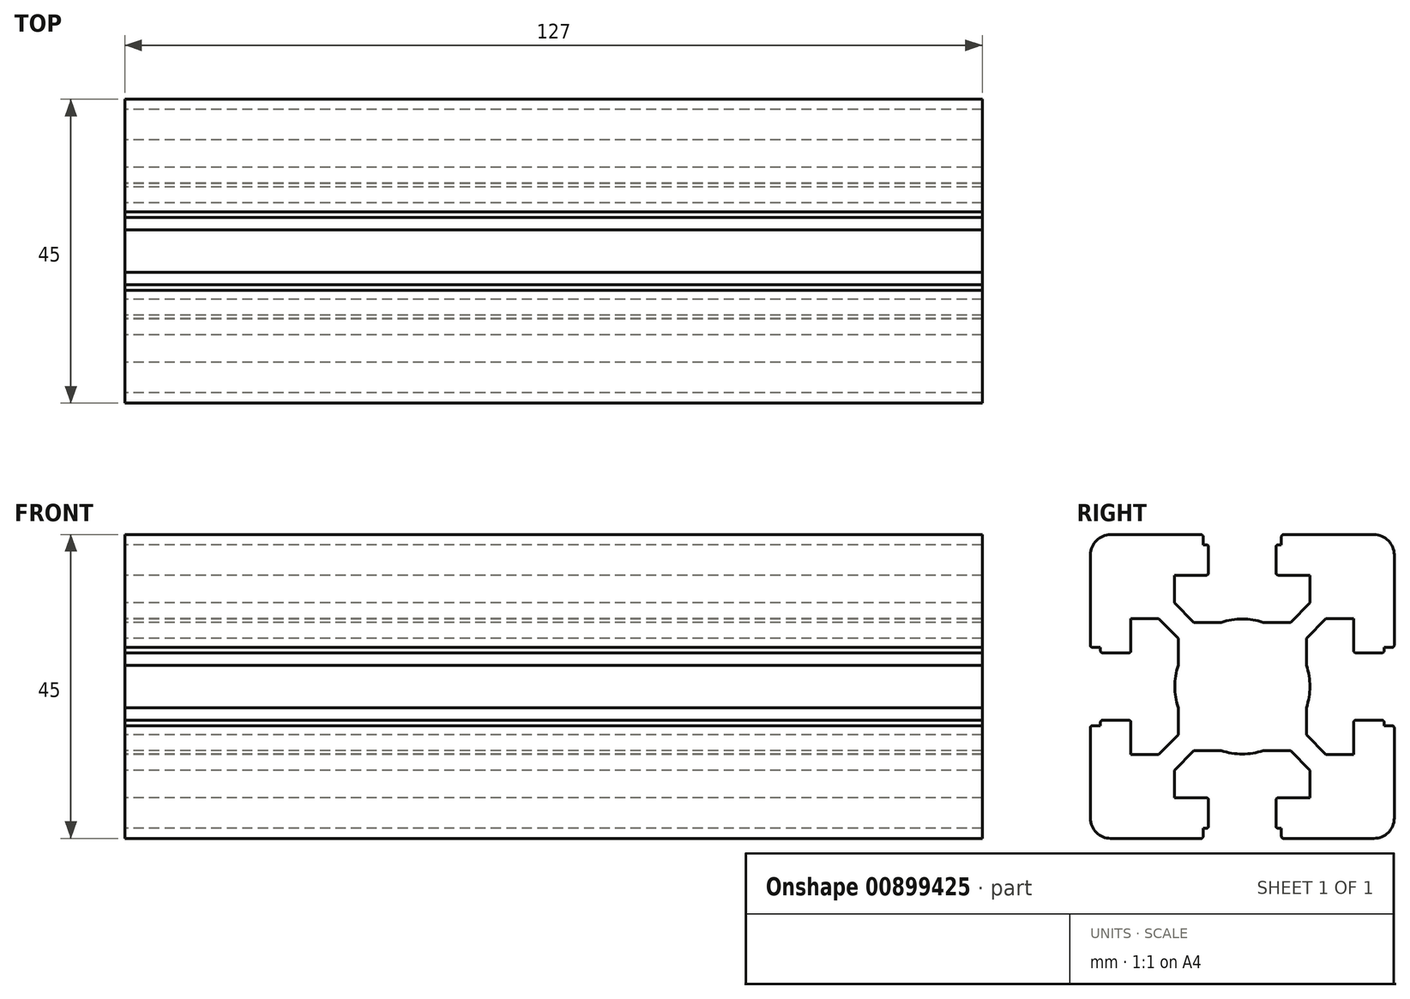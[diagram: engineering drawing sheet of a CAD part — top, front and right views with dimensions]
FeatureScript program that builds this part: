
annotation { "Feature Type Name" : "Feature", "Feature Type Description" : "" }
export const myFeature = defineFeature(function(context is Context, id is Id, definition is map)
    precondition{}
    {
        {
            var Q0;
            Q0=qCreatedBy(makeId("Right.planeOp"),FACE);
            var sketch = newSketch(context, id + "F0", { "sketchPlane" : qUnion([Q0])});
            skLineSegment(sketch, "E0", {"start": v(-20.09, -10.29) * mm, "end": v(-21.29, -10.29) * mm});
            skArc(sketch, "E1", {"start": v(-21.29, -10.29) * mm, "mid": v(-21.5, -10.38) * mm, "end": v(-21.59, -10.59) * mm});
            skLineSegment(sketch, "E2", {"start": v(-21.59, -10.59) * mm, "end": v(-21.59, -23.99) * mm});
            skArc(sketch, "E3", {"start": v(-21.59, -23.99) * mm, "mid": v(-20.7, -26.11) * mm, "end": v(-18.59, -26.99) * mm});
            skLineSegment(sketch, "E4", {"start": v(-18.59, -26.99) * mm, "end": v(-5.19, -26.99) * mm});
            skArc(sketch, "E5", {"start": v(-5.19, -26.99) * mm, "mid": v(-4.98, -26.9) * mm, "end": v(-4.89, -26.69) * mm});
            skLineSegment(sketch, "E6", {"start": v(-4.89, -26.69) * mm, "end": v(-4.89, -25.49) * mm});
            skLineSegment(sketch, "E7", {"start": v(-4.89, -25.49) * mm, "end": v(-4.39, -25.49) * mm});
            skArc(sketch, "E8", {"start": v(-4.39, -25.49) * mm, "mid": v(-4.18, -25.4) * mm, "end": v(-4.09, -25.19) * mm});
            skLineSegment(sketch, "E9", {"start": v(-4.09, -25.19) * mm, "end": v(-4.09, -21.29) * mm});
            skArc(sketch, "E10", {"start": v(-4.09, -21.29) * mm, "mid": v(-4.18, -21.08) * mm, "end": v(-4.39, -20.99) * mm});
            skLineSegment(sketch, "E11", {"start": v(-4.39, -20.99) * mm, "end": v(-9.14, -20.99) * mm});
            skLineSegment(sketch, "E12", {"start": v(-9.14, -20.99) * mm, "end": v(-9.14, -16.88) * mm});
            skLineSegment(sketch, "E13", {"start": v(-9.14, -16.88) * mm, "end": v(-6.25, -13.99) * mm});
            skLineSegment(sketch, "E14", {"start": v(-6.25, -13.99) * mm, "end": v(-2.21, -13.99) * mm});
            skArc(sketch, "E15", {"start": v(-2.21, -13.99) * mm, "mid": v(0.91, -14.49) * mm, "end": v(4.03, -13.99) * mm});
            skLineSegment(sketch, "E16", {"start": v(-20.09, -10.29) * mm, "end": v(-20.09, -9.79) * mm});
            skArc(sketch, "E17", {"start": v(-20.09, -9.79) * mm, "mid": v(-20, -9.58) * mm, "end": v(-19.79, -9.49) * mm});
            skLineSegment(sketch, "E18", {"start": v(-19.79, -9.49) * mm, "end": v(-15.89, -9.49) * mm});
            skArc(sketch, "E19", {"start": v(-15.89, -9.49) * mm, "mid": v(-15.68, -9.58) * mm, "end": v(-15.59, -9.79) * mm});
            skLineSegment(sketch, "E20", {"start": v(-15.59, -9.79) * mm, "end": v(-15.59, -14.54) * mm});
            skLineSegment(sketch, "E21", {"start": v(-15.59, -14.54) * mm, "end": v(-11.48, -14.54) * mm});
            skLineSegment(sketch, "E22", {"start": v(-11.48, -14.54) * mm, "end": v(-8.59, -11.65) * mm});
            skLineSegment(sketch, "E23", {"start": v(-8.59, -11.65) * mm, "end": v(-8.59, -7.61) * mm});
            skLineSegment(sketch, "E24", {"start": v(29.82, -4.49) * mm, "end": v(-31.05, -4.49) * mm});
            skLineSegment(sketch, "E25.MirrorCS", {"start": v(6.71, -25.49) * mm, "end": v(6.21, -25.49) * mm});
            skArc(sketch, "E26.MirrorCS", {"start": v(7.01, -26.99) * mm, "mid": v(6.8, -26.9) * mm, "end": v(6.71, -26.69) * mm});
            skLineSegment(sketch, "E27.MirrorCS", {"start": v(10.41, -11.65) * mm, "end": v(10.41, -7.61) * mm});
            skArc(sketch, "E28.MirrorCS", {"start": v(6.21, -25.49) * mm, "mid": v(6, -25.4) * mm, "end": v(5.91, -25.19) * mm});
            skLineSegment(sketch, "E29.MirrorCS", {"start": v(6.71, -26.69) * mm, "end": v(6.71, -25.49) * mm});
            skArc(sketch, "E30.MirrorCS", {"start": v(5.91, -21.29) * mm, "mid": v(6, -21.08) * mm, "end": v(6.21, -20.99) * mm});
            skLineSegment(sketch, "E31.MirrorCS", {"start": v(10.96, -16.88) * mm, "end": v(8.07, -13.99) * mm});
            skLineSegment(sketch, "E32.MirrorCS", {"start": v(13.3, -14.54) * mm, "end": v(10.41, -11.65) * mm});
            skLineSegment(sketch, "E33.MirrorCS", {"start": v(17.41, -14.54) * mm, "end": v(13.3, -14.54) * mm});
            skLineSegment(sketch, "E34.MirrorCS", {"start": v(17.41, -9.79) * mm, "end": v(17.41, -14.54) * mm});
            skLineSegment(sketch, "E35.MirrorCS", {"start": v(6.21, -20.99) * mm, "end": v(10.96, -20.99) * mm});
            skLineSegment(sketch, "E36.MirrorCS", {"start": v(8.07, -13.99) * mm, "end": v(4.03, -13.99) * mm});
            skArc(sketch, "E37.MirrorCS", {"start": v(4.03, -13.99) * mm, "mid": v(0.91, -14.49) * mm, "end": v(-2.21, -13.99) * mm});
            skLineSegment(sketch, "E38.MirrorCS", {"start": v(10.96, -20.99) * mm, "end": v(10.96, -16.88) * mm});
            skLineSegment(sketch, "E39.MirrorCS", {"start": v(5.91, -25.19) * mm, "end": v(5.91, -21.29) * mm});
            skArc(sketch, "E40.MirrorCS", {"start": v(23.41, -23.99) * mm, "mid": v(22.53, -26.11) * mm, "end": v(20.41, -26.99) * mm});
            skLineSegment(sketch, "E41.MirrorCS", {"start": v(20.41, -26.99) * mm, "end": v(7.01, -26.99) * mm});
            skLineSegment(sketch, "E42.MirrorCS", {"start": v(23.41, -10.59) * mm, "end": v(23.41, -23.99) * mm});
            skArc(sketch, "E43.MirrorCS", {"start": v(17.71, -9.49) * mm, "mid": v(17.5, -9.58) * mm, "end": v(17.41, -9.79) * mm});
            skArc(sketch, "E44.MirrorCS", {"start": v(23.11, -10.29) * mm, "mid": v(23.32, -10.38) * mm, "end": v(23.41, -10.59) * mm});
            skLineSegment(sketch, "E45.MirrorCS", {"start": v(21.91, -10.29) * mm, "end": v(21.91, -9.79) * mm});
            skLineSegment(sketch, "E46.MirrorCS", {"start": v(21.91, -10.29) * mm, "end": v(23.11, -10.29) * mm});
            skArc(sketch, "E47.MirrorCS", {"start": v(21.91, -9.79) * mm, "mid": v(21.82, -9.58) * mm, "end": v(21.61, -9.49) * mm});
            skLineSegment(sketch, "E48.MirrorCS", {"start": v(21.61, -9.49) * mm, "end": v(17.71, -9.49) * mm});
            skLineSegment(sketch, "E49.MirrorCS", {"start": v(6.71, 16.51) * mm, "end": v(6.21, 16.51) * mm});
            skArc(sketch, "E50.MirrorCS", {"start": v(-4.39, 16.51) * mm, "mid": v(-4.18, 16.42) * mm, "end": v(-4.09, 16.21) * mm});
            skLineSegment(sketch, "E51.MirrorCS", {"start": v(-4.89, 16.51) * mm, "end": v(-4.39, 16.51) * mm});
            skArc(sketch, "E52.MirrorCS", {"start": v(5.91, 12.31) * mm, "mid": v(6, 12.1) * mm, "end": v(6.21, 12.01) * mm});
            skLineSegment(sketch, "E53.MirrorCS", {"start": v(6.71, 17.71) * mm, "end": v(6.71, 16.51) * mm});
            skLineSegment(sketch, "E54.MirrorCS", {"start": v(-4.89, 17.71) * mm, "end": v(-4.89, 16.51) * mm});
            skArc(sketch, "E55.MirrorCS", {"start": v(-5.19, 18.01) * mm, "mid": v(-4.98, 17.92) * mm, "end": v(-4.89, 17.71) * mm});
            skArc(sketch, "E56.MirrorCS", {"start": v(-4.09, 12.31) * mm, "mid": v(-4.18, 12.1) * mm, "end": v(-4.39, 12.01) * mm});
            skArc(sketch, "E57.MirrorCS", {"start": v(7.01, 18.01) * mm, "mid": v(6.8, 17.92) * mm, "end": v(6.71, 17.71) * mm});
            skArc(sketch, "E58.MirrorCS", {"start": v(6.21, 16.51) * mm, "mid": v(6, 16.42) * mm, "end": v(5.91, 16.21) * mm});
            skArc(sketch, "E59.MirrorCS", {"start": v(23.11, 1.31) * mm, "mid": v(23.32, 1.4) * mm, "end": v(23.41, 1.61) * mm});
            skLineSegment(sketch, "E60.MirrorCS", {"start": v(21.91, 1.31) * mm, "end": v(21.91, 0.81) * mm});
            skArc(sketch, "E61.MirrorCS", {"start": v(-15.89, 0.51) * mm, "mid": v(-15.68, 0.6) * mm, "end": v(-15.59, 0.81) * mm});
            skArc(sketch, "E62.MirrorCS", {"start": v(-21.29, 1.31) * mm, "mid": v(-21.5, 1.4) * mm, "end": v(-21.59, 1.61) * mm});
            skArc(sketch, "E63.MirrorCS", {"start": v(17.71, 0.51) * mm, "mid": v(17.5, 0.6) * mm, "end": v(17.41, 0.81) * mm});
            skArc(sketch, "E64.MirrorCS", {"start": v(21.91, 0.81) * mm, "mid": v(21.82, 0.6) * mm, "end": v(21.61, 0.51) * mm});
            skLineSegment(sketch, "E65.MirrorCS", {"start": v(21.91, 1.31) * mm, "end": v(23.11, 1.31) * mm});
            skArc(sketch, "E66.MirrorCS", {"start": v(14.31, 5.31) * mm, "mid": v(14.1, 5.4) * mm, "end": v(14.01, 5.61) * mm});
            skArc(sketch, "E67.MirrorCS", {"start": v(-20.09, 0.81) * mm, "mid": v(-20, 0.6) * mm, "end": v(-19.79, 0.51) * mm});
            skLineSegment(sketch, "E68.MirrorCS", {"start": v(-20.09, 1.31) * mm, "end": v(-21.29, 1.31) * mm});
            skLineSegment(sketch, "E69.MirrorCS", {"start": v(-20.09, 1.31) * mm, "end": v(-20.09, 0.81) * mm});
            skLineSegment(sketch, "E70.MirrorCS", {"start": v(8.07, 5.01) * mm, "end": v(4.03, 5.01) * mm});
            skLineSegment(sketch, "E71.MirrorCS", {"start": v(-4.09, 16.21) * mm, "end": v(-4.09, 12.31) * mm});
            skLineSegment(sketch, "E72.MirrorCS", {"start": v(-9.14, 12.01) * mm, "end": v(-9.14, 7.9) * mm});
            skLineSegment(sketch, "E73.MirrorCS", {"start": v(-15.59, 5.56) * mm, "end": v(-11.48, 5.56) * mm});
            skLineSegment(sketch, "E74.MirrorCS", {"start": v(-4.39, 12.01) * mm, "end": v(-9.14, 12.01) * mm});
            skLineSegment(sketch, "E75.MirrorCS", {"start": v(-9.14, 7.9) * mm, "end": v(-6.25, 5.01) * mm});
            skLineSegment(sketch, "E76.MirrorCS", {"start": v(10.96, 12.01) * mm, "end": v(10.96, 7.9) * mm});
            skArc(sketch, "E77.MirrorCS", {"start": v(-21.59, 15.01) * mm, "mid": v(-20.7, 17.13) * mm, "end": v(-18.59, 18.01) * mm});
            skLineSegment(sketch, "E78.MirrorCS", {"start": v(23.41, 1.61) * mm, "end": v(23.41, 15.01) * mm});
            skLineSegment(sketch, "E79.MirrorCS", {"start": v(13.3, 5.56) * mm, "end": v(10.41, 2.67) * mm});
            skLineSegment(sketch, "E80.MirrorCS", {"start": v(-8.59, 2.67) * mm, "end": v(-8.59, -1.37) * mm});
            skLineSegment(sketch, "E81.MirrorCS", {"start": v(-15.59, 0.81) * mm, "end": v(-15.59, 5.56) * mm});
            skLineSegment(sketch, "E82.MirrorCS", {"start": v(10.41, 2.67) * mm, "end": v(10.41, -1.37) * mm});
            skLineSegment(sketch, "E83.MirrorCS", {"start": v(-18.59, 18.01) * mm, "end": v(-5.19, 18.01) * mm});
            skLineSegment(sketch, "E84.MirrorCS", {"start": v(10.96, 7.9) * mm, "end": v(8.07, 5.01) * mm});
            skLineSegment(sketch, "E85.MirrorCS", {"start": v(17.41, 5.56) * mm, "end": v(13.3, 5.56) * mm});
            skArc(sketch, "E86.MirrorCS", {"start": v(23.41, 15.01) * mm, "mid": v(22.53, 17.13) * mm, "end": v(20.41, 18.01) * mm});
            skLineSegment(sketch, "E87.MirrorCS", {"start": v(5.91, 16.21) * mm, "end": v(5.91, 12.31) * mm});
            skLineSegment(sketch, "E88.MirrorCS", {"start": v(17.41, 0.81) * mm, "end": v(17.41, 5.56) * mm});
            skLineSegment(sketch, "E89.MirrorCS", {"start": v(-11.48, 5.56) * mm, "end": v(-8.59, 2.67) * mm});
            skLineSegment(sketch, "E90.MirrorCS", {"start": v(-6.25, 5.01) * mm, "end": v(-2.21, 5.01) * mm});
            skLineSegment(sketch, "E91.MirrorCS", {"start": v(-21.59, 1.61) * mm, "end": v(-21.59, 15.01) * mm});
            skArc(sketch, "E92.MirrorCS", {"start": v(4.03, 5.01) * mm, "mid": v(0.91, 5.51) * mm, "end": v(-2.21, 5.01) * mm});
            skLineSegment(sketch, "E93.MirrorCS", {"start": v(6.21, 12.01) * mm, "end": v(10.96, 12.01) * mm});
            skArc(sketch, "E94.MirrorCS", {"start": v(-2.21, 5.01) * mm, "mid": v(0.91, 5.51) * mm, "end": v(4.03, 5.01) * mm});
            skLineSegment(sketch, "E95.MirrorCS", {"start": v(20.41, 18.01) * mm, "end": v(7.01, 18.01) * mm});
            skLineSegment(sketch, "E96.MirrorCS", {"start": v(-19.79, 0.51) * mm, "end": v(-15.89, 0.51) * mm});
            skLineSegment(sketch, "E97.MirrorCS", {"start": v(21.61, 0.51) * mm, "end": v(17.71, 0.51) * mm});
            skLineSegment(sketch, "E98.MirrorCS", {"start": v(0.91, -27.65) * mm, "end": v(0.91, 19.82) * mm});
            skArc(sketch, "E99", {"start": v(-8.59, -1.37) * mm, "mid": v(-9.09, -4.49) * mm, "end": v(-8.59, -7.61) * mm});
            skArc(sketch, "E100", {"start": v(10.41, -7.61) * mm, "mid": v(10.91, -4.49) * mm, "end": v(10.41, -1.37) * mm});
            skSolve(sketch);
        }
        {
            var Q0;
            Q0=qSketchRegion(id+"F0",true);
            extrude(context, id + "F1", {"entities" : qUnion([Q0]), "depth" : 127 * mm, "offsetDistance" : 25.4 * mm});
        }
    });
